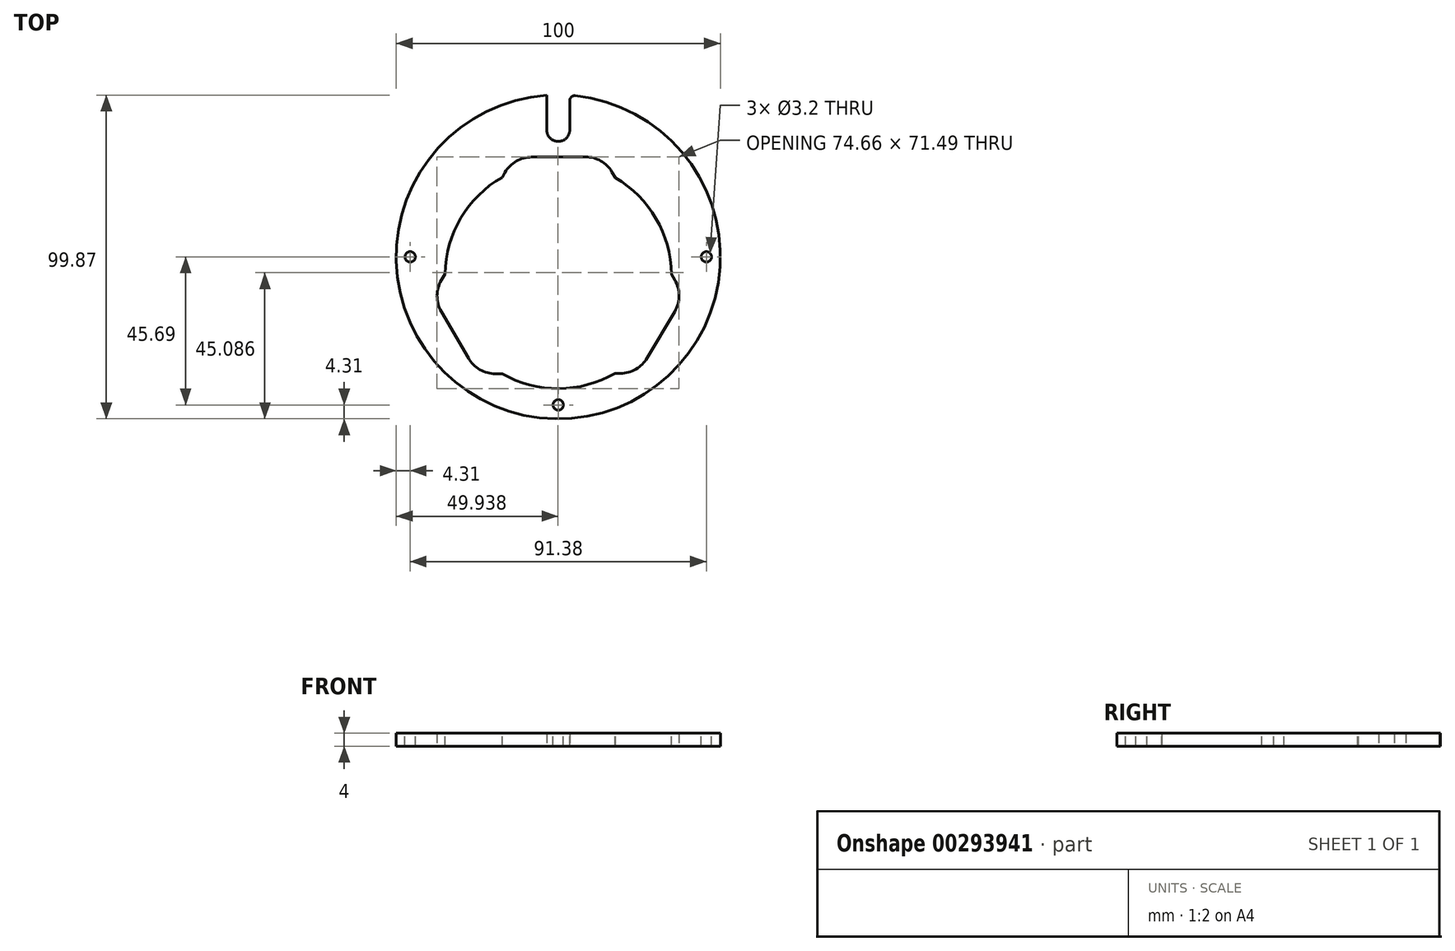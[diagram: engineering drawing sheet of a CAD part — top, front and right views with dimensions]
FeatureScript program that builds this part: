
annotation { "Feature Type Name" : "Feature", "Feature Type Description" : "" }
export const myFeature = defineFeature(function(context is Context, id is Id, definition is map)
    precondition{}
    {
        {
            var Q0;
            Q0=qCreatedBy(makeId("Top.planeOp"),FACE);
            var sketch = newSketch(context, id + "F0", { "sketchPlane" : qUnion([Q0])});
            skArc(sketch, "E0", {"start": v(-43.11, 25.33) * mm, "mid": v(23.28, -44.25) * mm, "end": v(3.55, 49.87) * mm});
            skLineSegment(sketch, "E1.1", {"start": v(-16.43, 26.04) * mm, "end": v(-36.05, -7.16) * mm});
            skLineSegment(sketch, "E1.3", {"start": v(8.47, 30.83) * mm, "end": v(-8.18, 30.77) * mm});
            skLineSegment(sketch, "E1.4", {"start": v(19.2, -35.93) * mm, "end": v(-19.36, -36.07) * mm});
            skLineSegment(sketch, "E2", {"start": v(27.46, -31.2) * mm, "end": v(35.93, -16.88) * mm});
            skLineSegment(sketch, "E3", {"start": v(35.96, -7.14) * mm, "end": v(16.56, 26.2) * mm});
            skLineSegment(sketch, "E4", {"start": v(-27.71, -31.28) * mm, "end": v(-36.09, -16.9) * mm});
            skLineSegment(sketch, "E5", {"start": v(0.1, 30.8) * mm, "end": v(-0.12, -36) * mm, "construction": true});
            skPoint(sketch, "E6.visualSharp", {"position": v(13.85, 30.85) * mm});
            skArc(sketch, "E6.filletArc", {"start": v(16.56, 26.2) * mm, "mid": v(13.14, 29.6) * mm, "end": v(8.47, 30.83) * mm});
            skPoint(sketch, "E7.visualSharp", {"position": v(-13.65, 30.75) * mm});
            skArc(sketch, "E7.filletArc", {"start": v(-8.18, 30.77) * mm, "mid": v(-12.93, 29.5) * mm, "end": v(-16.43, 26.04) * mm});
            skPoint(sketch, "E8.visualSharp", {"position": v(-38.93, -12.02) * mm});
            skArc(sketch, "E8.filletArc", {"start": v(-36.05, -7.16) * mm, "mid": v(-37.4, -12.02) * mm, "end": v(-36.09, -16.9) * mm});
            skPoint(sketch, "E9.visualSharp", {"position": v(-24.92, -36.09) * mm});
            skArc(sketch, "E9.filletArc", {"start": v(-27.71, -31.28) * mm, "mid": v(-24.18, -34.8) * mm, "end": v(-19.36, -36.07) * mm});
            skPoint(sketch, "E10.visualSharp", {"position": v(24.68, -35.92) * mm});
            skArc(sketch, "E10.filletArc", {"start": v(19.2, -35.93) * mm, "mid": v(23.96, -34.66) * mm, "end": v(27.46, -31.2) * mm});
            skPoint(sketch, "E11.visualSharp", {"position": v(38.8, -12.02) * mm});
            skArc(sketch, "E11.filletArc", {"start": v(35.93, -16.88) * mm, "mid": v(37.27, -12.01) * mm, "end": v(35.96, -7.14) * mm});
            skArc(sketch, "E12.trimOffspring", {"start": v(-39.08, 31.2) * mm, "mid": v(-0.17, -50) * mm, "end": v(39.29, 30.93) * mm});
            skArc(sketch, "E13.trimOffspring", {"start": v(39.29, 30.93) * mm, "mid": v(23.42, 44.18) * mm, "end": v(3.55, 49.87) * mm});
            skArc(sketch, "E14", {"start": v(-3.55, 39.24) * mm, "mid": v(0, 35.6) * mm, "end": v(3.55, 39.24) * mm});
            skLineSegment(sketch, "E15", {"start": v(3.55, 39.24) * mm, "end": v(3.55, 49.87) * mm});
            skLineSegment(sketch, "E16", {"start": v(-3.55, 39.24) * mm, "end": v(-3.55, 49.87) * mm});
            skArc(sketch, "E17.trimOffspring", {"start": v(-3.55, 49.87) * mm, "mid": v(-23.27, 44.25) * mm, "end": v(-39.08, 31.2) * mm});
            skArc(sketch, "E18.trimOffspring", {"start": v(-3.55, 49.87) * mm, "mid": v(-20, 45.83) * mm, "end": v(-34.15, 36.52) * mm});
            skSolve(sketch);
        }
        {
            var Q0;
            Q0 = qSketchRegion(id + "F0", true);
            extrude(context, id + "F1", {"entities" : qUnion([Q0]), "depth" : 4 * mm, "offsetDistance" : 25 * mm});
        }
        {
            var Q0;
            Q0=makeQuery(id+"F1.opExtrude","SWEPT_EDGE",EDGE,{"disambiguationData":[OSD([sQuery(id+"F0.wireOp",EDGE,"E12.trimOffspring"),sQuery(id+"F0.wireOp",EDGE,"6c727b06-af09-4e90-8dae-46ab04d820b60.MirrorCS")])]});
            var Q1;
            Q1=makeQuery(id+"F1.opExtrude","SWEPT_EDGE",EDGE,{"disambiguationData":[OSD([sQuery(id+"F0.wireOp",EDGE,"805600f7-c122-4390-a8df-b2e744f2050e0.MirrorCS"),sQuery(id+"F0.wireOp",EDGE,"8a93d002-24a3-456d-b69f-58e1eb542867.trimOffspring")])]});
            var Q2;
            Q2=makeQuery(id+"F1.opExtrude","SWEPT_EDGE",EDGE,{"disambiguationData":[OSD([sQuery(id+"F0.wireOp",EDGE,"38ea3989-21a6-425a-b182-32b45d782dfe3.MirrorCS"),sQuery(id+"F0.wireOp",EDGE,"8a93d002-24a3-456d-b69f-58e1eb542867.trimOffspring")])]});
            var Q3;
            Q3=makeQuery(id+"F1.opExtrude","SWEPT_EDGE",EDGE,{"disambiguationData":[OSD([sQuery(id+"F0.wireOp",EDGE,"38ea3989-21a6-425a-b182-32b45d782dfe1.MirrorCS"),sQuery(id+"F0.wireOp",EDGE,"E13.trimOffspring")])]});
            var Q4;
            Q4=makeQuery(id+"F1.opExtrude","SWEPT_EDGE",EDGE,{"disambiguationData":[OSD([sQuery(id+"F0.wireOp",EDGE,"E0"),sQuery(id+"F0.wireOp",EDGE,"LhtLjBrC-eomG-5qtl-8ASw-Hag512C7QlKN")])]});
            var Q5;
            Q5=makeQuery(id+"F1.opExtrude","SWEPT_EDGE",EDGE,{"disambiguationData":[OSD([sQuery(id+"F0.wireOp",EDGE,"6gVIOyo9-SYRj-CiXB-pLlF-RIEQTlMOgRB0"),sQuery(id+"F0.wireOp",EDGE,"E13.trimOffspring")])]});
            var Q6;
            Q6=makeQuery(id+"F1.opExtrude","SWEPT_EDGE",EDGE,{"disambiguationData":[OSD([sQuery(id+"F0.wireOp",EDGE,"E0"),sQuery(id+"F0.wireOp",EDGE,"ISlZrfTa-9Kd0-3l5e-JYQw-XVVApxpbAIzY")])]});
            var Q7;
            Q7=makeQuery(id+"F1.opExtrude","SWEPT_EDGE",EDGE,{"disambiguationData":[OSD([sQuery(id+"F0.wireOp",EDGE,"MqOhkdVH-UTDp-6l4v-qCBS-gve57MoHbj08"),sQuery(id+"F0.wireOp",EDGE,"E12.trimOffspring")])]});
            fillet(context, id + "F2", {"entities" : qUnion([Q0, Q1, Q2, Q3, Q4, Q5, Q6, Q7]), "tangentPropagation" : true, "radius" : 1.5 * mm, "defaultsChanged" : false, "vertexSettings" : [], "allowEdgeOverflow" : false});
        }
        {
            var Q0;
            Q0=makeQuery(id+"F1.opExtrude","CAP_FACE",FACE,{"disambiguationData":[OSD([sQuery(id+"F0.wireOp",EDGE,"E0"),sQuery(id+"F0.wireOp",EDGE,"E1.1"),sQuery(id+"F0.wireOp",EDGE,"E1.3"),sQuery(id+"F0.wireOp",EDGE,"E1.4"),sQuery(id+"F0.wireOp",EDGE,"E2"),sQuery(id+"F0.wireOp",EDGE,"E3"),sQuery(id+"F0.wireOp",EDGE,"E4"),sQuery(id+"F0.wireOp",EDGE,"E6.filletArc"),sQuery(id+"F0.wireOp",EDGE,"E7.filletArc"),sQuery(id+"F0.wireOp",EDGE,"E8.filletArc"),sQuery(id+"F0.wireOp",EDGE,"E9.filletArc"),sQuery(id+"F0.wireOp",EDGE,"E10.filletArc"),sQuery(id+"F0.wireOp",EDGE,"E11.filletArc"),sQuery(id+"F0.wireOp",EDGE,"CBBoCosa-OUW0-Y7Qp-MoIT-tpmoWdFkD8ja"),sQuery(id+"F0.wireOp",EDGE,"wuFyAzv8-E2dn-3uYP-GQZm-P3b3cEF6jcgd"),sQuery(id+"F0.wireOp",EDGE,"ISlZrfTa-9Kd0-3l5e-JYQw-XVVApxpbAIzY"),sQuery(id+"F0.wireOp",EDGE,"MqOhkdVH-UTDp-6l4v-qCBS-gve57MoHbj08"),sQuery(id+"F0.wireOp",EDGE,"6gVIOyo9-SYRj-CiXB-pLlF-RIEQTlMOgRB0"),sQuery(id+"F0.wireOp",EDGE,"LhtLjBrC-eomG-5qtl-8ASw-Hag512C7QlKN"),sQuery(id+"F0.wireOp",EDGE,"E12.trimOffspring"),sQuery(id+"F0.wireOp",EDGE,"38ea3989-21a6-425a-b182-32b45d782dfe0.MirrorCS"),sQuery(id+"F0.wireOp",EDGE,"38ea3989-21a6-425a-b182-32b45d782dfe1.MirrorCS"),sQuery(id+"F0.wireOp",EDGE,"38ea3989-21a6-425a-b182-32b45d782dfe2.MirrorCS"),sQuery(id+"F0.wireOp",EDGE,"38ea3989-21a6-425a-b182-32b45d782dfe3.MirrorCS"),sQuery(id+"F0.wireOp",EDGE,"805600f7-c122-4390-a8df-b2e744f2050e0.MirrorCS"),sQuery(id+"F0.wireOp",EDGE,"6c727b06-af09-4e90-8dae-46ab04d820b60.MirrorCS"),sQuery(id+"F0.wireOp",EDGE,"E13.trimOffspring"),sQuery(id+"F0.wireOp",EDGE,"8a93d002-24a3-456d-b69f-58e1eb542867.trimOffspring")])],"isStart":false});
            var sketch = newSketch(context, id + "F3", { "sketchPlane" : qUnion([Q0])});
            skCircle(sketch, "E19", {"center": v(0, 45.7) * mm, "radius": 1.6 * mm});
            skCircle(sketch, "E20.1.0", {"center": v(-45.7, 0) * mm, "radius": 1.6 * mm});
            skCircle(sketch, "E20.2.0", {"center": v(0, -45.7) * mm, "radius": 1.6 * mm});
            skCircle(sketch, "E20.3.0", {"center": v(45.7, 0) * mm, "radius": 1.6 * mm});
            skPoint(sketch, "E20.center", {"position": v(0, 0) * mm});
            skSolve(sketch);
        }
        {
            var Q0;
            Q0 = qSketchRegion(id + "F3", true);
            extrude(context, id + "F4", {"entities" : qUnion([Q0]), "operationType" : NewBodyOperationType.REMOVE, "endBound" : BoundingType.THROUGH_ALL, "oppositeDirection" : true, "depth" : 25 * mm, "offsetDistance" : 25 * mm});
        }
        {
            var Q0;
            Q0=makeQuery(id+"F1.opExtrude","CAP_FACE",FACE,{"disambiguationData":[OSD([sQuery(id+"F0.wireOp",EDGE,"E0"),sQuery(id+"F0.wireOp",EDGE,"E1.1"),sQuery(id+"F0.wireOp",EDGE,"E1.3"),sQuery(id+"F0.wireOp",EDGE,"E1.4"),sQuery(id+"F0.wireOp",EDGE,"E2"),sQuery(id+"F0.wireOp",EDGE,"E3"),sQuery(id+"F0.wireOp",EDGE,"E4"),sQuery(id+"F0.wireOp",EDGE,"E6.filletArc"),sQuery(id+"F0.wireOp",EDGE,"E7.filletArc"),sQuery(id+"F0.wireOp",EDGE,"E8.filletArc"),sQuery(id+"F0.wireOp",EDGE,"E9.filletArc"),sQuery(id+"F0.wireOp",EDGE,"E10.filletArc"),sQuery(id+"F0.wireOp",EDGE,"E11.filletArc"),sQuery(id+"F0.wireOp",EDGE,"CBBoCosa-OUW0-Y7Qp-MoIT-tpmoWdFkD8ja"),sQuery(id+"F0.wireOp",EDGE,"wuFyAzv8-E2dn-3uYP-GQZm-P3b3cEF6jcgd"),sQuery(id+"F0.wireOp",EDGE,"ISlZrfTa-9Kd0-3l5e-JYQw-XVVApxpbAIzY"),sQuery(id+"F0.wireOp",EDGE,"MqOhkdVH-UTDp-6l4v-qCBS-gve57MoHbj08"),sQuery(id+"F0.wireOp",EDGE,"6gVIOyo9-SYRj-CiXB-pLlF-RIEQTlMOgRB0"),sQuery(id+"F0.wireOp",EDGE,"LhtLjBrC-eomG-5qtl-8ASw-Hag512C7QlKN"),sQuery(id+"F0.wireOp",EDGE,"E12.trimOffspring"),sQuery(id+"F0.wireOp",EDGE,"38ea3989-21a6-425a-b182-32b45d782dfe0.MirrorCS"),sQuery(id+"F0.wireOp",EDGE,"38ea3989-21a6-425a-b182-32b45d782dfe1.MirrorCS"),sQuery(id+"F0.wireOp",EDGE,"38ea3989-21a6-425a-b182-32b45d782dfe2.MirrorCS"),sQuery(id+"F0.wireOp",EDGE,"38ea3989-21a6-425a-b182-32b45d782dfe3.MirrorCS"),sQuery(id+"F0.wireOp",EDGE,"805600f7-c122-4390-a8df-b2e744f2050e0.MirrorCS"),sQuery(id+"F0.wireOp",EDGE,"6c727b06-af09-4e90-8dae-46ab04d820b60.MirrorCS"),sQuery(id+"F0.wireOp",EDGE,"E13.trimOffspring"),sQuery(id+"F0.wireOp",EDGE,"8a93d002-24a3-456d-b69f-58e1eb542867.trimOffspring")])],"isStart":false});
            var sketch = newSketch(context, id + "F5", { "sketchPlane" : qUnion([Q0])});
            skLineSegment(sketch, "E21", {"start": v(31.7, -24.04) * mm, "end": v(-26.24, 9.44) * mm, "construction": true});
            skLineSegment(sketch, "E22", {"start": v(26.26, 9.53) * mm, "end": v(-31.9, -24.32) * mm, "construction": true});
            skPoint(sketch, "E22.endSnap0", {"position": v(-31.9, -24.09) * mm});
            skPoint(sketch, "E23", {"position": v(0, -5.76) * mm});
            skCircle(sketch, "E24", {"center": v(0, -5.76) * mm, "radius": 34.9 * mm});
            skSolve(sketch);
        }
        {
            var Q0;
            Q0 = qSketchRegion(id + "F5", true);
            extrude(context, id + "F6", {"entities" : qUnion([Q0]), "operationType" : NewBodyOperationType.REMOVE, "endBound" : BoundingType.THROUGH_ALL, "oppositeDirection" : true, "depth" : 25 * mm, "offsetDistance" : 25 * mm});
        }
    });
